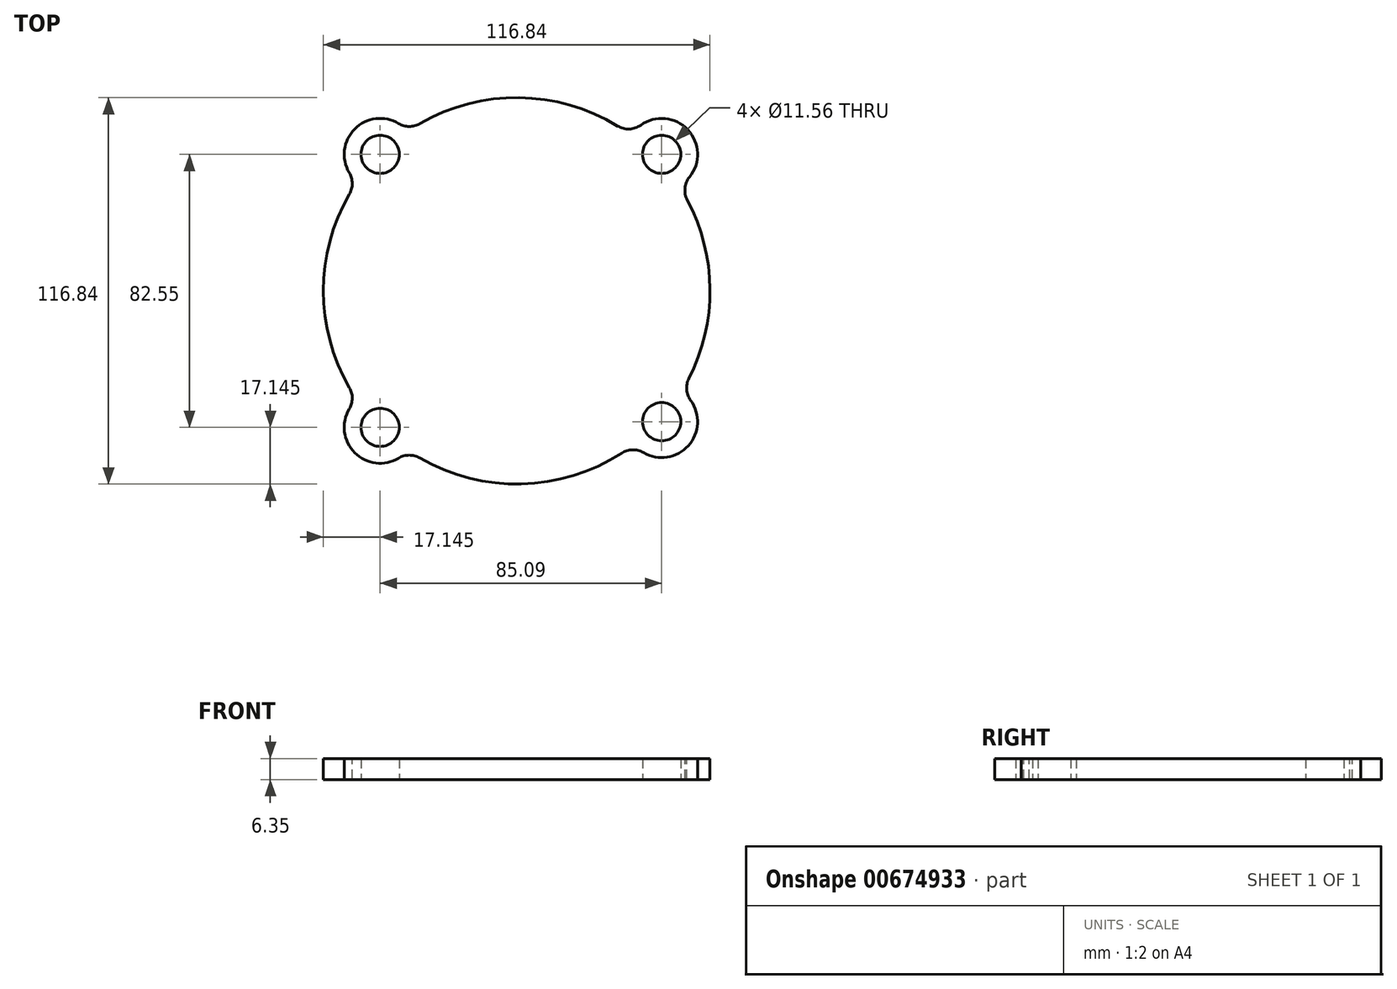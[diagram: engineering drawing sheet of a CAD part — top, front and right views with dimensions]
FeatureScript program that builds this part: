
annotation { "Feature Type Name" : "Feature", "Feature Type Description" : "" }
export const myFeature = defineFeature(function(context is Context, id is Id, definition is map)
    precondition{}
    {
        {
            var Q0;
            Q0=qCreatedBy(makeId("Top.planeOp"),FACE);
            var sketch = newSketch(context, id + "F0", { "sketchPlane" : qUnion([Q0])});
            skArc(sketch, "E0", {"start": v(-48.24, 32.95) * mm, "mid": v(-58.42, 0) * mm, "end": v(-48.24, -32.95) * mm});
            skCircle(sketch, "E1", {"center": v(-41.27, 41.28) * mm, "radius": 5.78 * mm});
            skCircle(sketch, "E2", {"center": v(43.82, 41.28) * mm, "radius": 5.78 * mm});
            skCircle(sketch, "E3", {"center": v(43.82, -39.56) * mm, "radius": 5.78 * mm});
            skCircle(sketch, "E4", {"center": v(-41.27, -41.28) * mm, "radius": 5.78 * mm});
            skArc(sketch, "E5", {"start": v(-32.92, 48.2) * mm, "mid": v(-48.95, 48.95) * mm, "end": v(-48.2, 32.92) * mm});
            skArc(sketch, "E6", {"start": v(49.04, 31.75) * mm, "mid": v(51.72, 48.72) * mm, "end": v(34.62, 47.05) * mm});
            skArc(sketch, "E7", {"start": v(35.43, -46.45) * mm, "mid": v(51.87, -46.84) * mm, "end": v(49.82, -30.51) * mm});
            skArc(sketch, "E8.trimOffspring", {"start": v(34.62, 47.05) * mm, "mid": v(1.03, 58.41) * mm, "end": v(-32.95, 48.24) * mm});
            skArc(sketch, "E9.trimOffspring", {"start": v(49.82, -30.51) * mm, "mid": v(58.42, 0.73) * mm, "end": v(49.04, 31.75) * mm});
            skArc(sketch, "E10.trimOffspring", {"start": v(-32.95, -48.24) * mm, "mid": v(1.53, -58.4) * mm, "end": v(35.43, -46.45) * mm});
            skArc(sketch, "E11", {"start": v(-48.24, -32.95) * mm, "mid": v(-48.95, -48.95) * mm, "end": v(-32.95, -48.24) * mm});
            skSolve(sketch);
        }
        {
            var Q0;
            {var subQ4=sQuery(id+"F0.wireOp",EDGE,"E0");Q0=makeQuery(id+"F0.imprint","IMPRINT",FACE,{"disambiguationData":[TD([[makeQuery(id+"F0.imprint","IMPRINT",EDGE,{"derivedFrom":subQ4}),1.0]])]});}
            extrude(context, id + "F1", {"entities" : qUnion([Q0]), "depth" : 6.35 * mm, "offsetDistance" : 25.4 * mm});
        }
        {
            var Q0;
            Q0=makeQuery(id+"F1.opExtrude","SWEPT_EDGE",EDGE,{"disambiguationData":[OSD([sQuery(id+"F0.wireOp",EDGE,"E0"),sQuery(id+"F0.wireOp",EDGE,"E5")])]});
            var Q1;
            Q1=makeQuery(id+"F1.opExtrude","SWEPT_EDGE",EDGE,{"disambiguationData":[OSD([sQuery(id+"F0.wireOp",EDGE,"E0"),sQuery(id+"F0.wireOp",EDGE,"knn74bfa-RRcG-CiZl-l36T-FFG7u0atq7rg")])]});
            var Q2;
            Q2=makeQuery(id+"F1.opExtrude","SWEPT_EDGE",EDGE,{"disambiguationData":[OSD([sQuery(id+"F0.wireOp",EDGE,"E7"),sQuery(id+"F0.wireOp",EDGE,"E10.trimOffspring")])]});
            var Q3;
            Q3=makeQuery(id+"F1.opExtrude","SWEPT_EDGE",EDGE,{"disambiguationData":[OSD([sQuery(id+"F0.wireOp",EDGE,"knn74bfa-RRcG-CiZl-l36T-FFG7u0atq7rg"),sQuery(id+"F0.wireOp",EDGE,"E10.trimOffspring")])]});
            var Q4;
            Q4=makeQuery(id+"F1.opExtrude","SWEPT_EDGE",EDGE,{"disambiguationData":[OSD([sQuery(id+"F0.wireOp",EDGE,"E7"),sQuery(id+"F0.wireOp",EDGE,"E9.trimOffspring")])]});
            var Q5;
            Q5=makeQuery(id+"F1.opExtrude","SWEPT_EDGE",EDGE,{"disambiguationData":[OSD([sQuery(id+"F0.wireOp",EDGE,"E5"),sQuery(id+"F0.wireOp",EDGE,"E8.trimOffspring")])]});
            var Q6;
            Q6=makeQuery(id+"F1.opExtrude","SWEPT_EDGE",EDGE,{"disambiguationData":[OSD([sQuery(id+"F0.wireOp",EDGE,"E6"),sQuery(id+"F0.wireOp",EDGE,"E8.trimOffspring")])]});
            var Q7;
            Q7=makeQuery(id+"F1.opExtrude","SWEPT_EDGE",EDGE,{"disambiguationData":[OSD([sQuery(id+"F0.wireOp",EDGE,"E6"),sQuery(id+"F0.wireOp",EDGE,"E9.trimOffspring")])]});
            fillet(context, id + "F2", {"entities" : qUnion([Q0, Q1, Q2, Q3, Q4, Q5, Q6, Q7]), "radius" : 6.35 * mm, "tangentPropagation" : true, "allowEdgeOverflow" : false});
        }
    });
